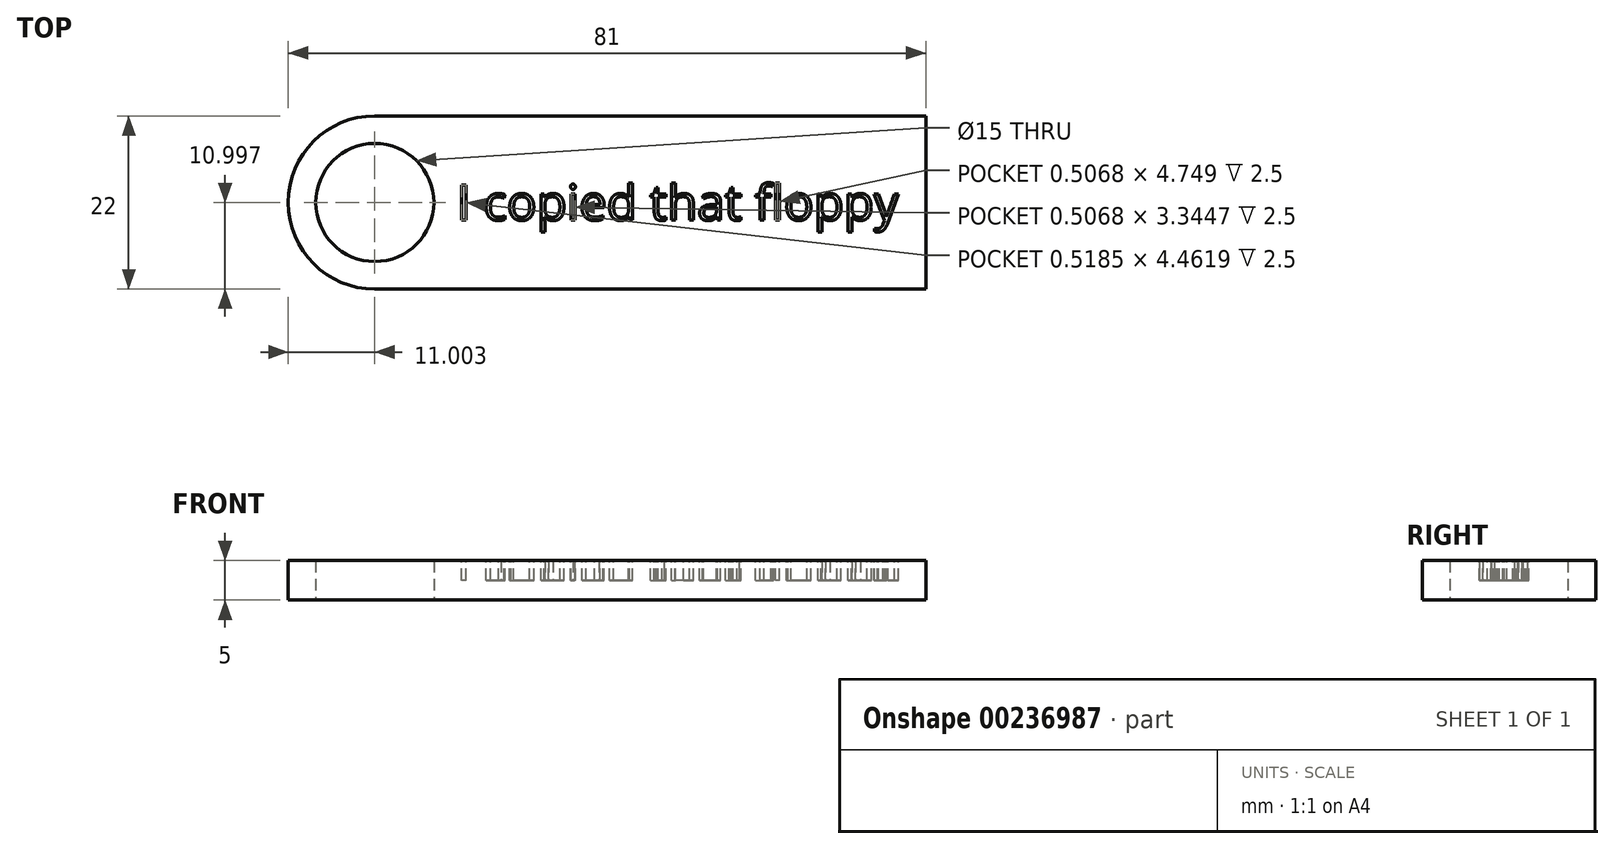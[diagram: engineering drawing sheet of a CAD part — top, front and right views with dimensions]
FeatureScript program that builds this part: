
annotation { "Feature Type Name" : "Feature", "Feature Type Description" : "" }
export const myFeature = defineFeature(function(context is Context, id is Id, definition is map)
    precondition{}
    {
        {
            var Q0;
            Q0=qCreatedBy(makeId("Top.planeOp"),FACE);
            var sketch = newSketch(context, id + "F0", { "sketchPlane" : qUnion([Q0])});
            skLineSegment(sketch, "E0", {"start": v(39.9, 37.37) * mm, "end": v(-30.1, 37.37) * mm});
            skLineSegment(sketch, "E1", {"start": v(39.9, 37.37) * mm, "end": v(39.9, 15.37) * mm});
            skLineSegment(sketch, "E2", {"start": v(39.9, 15.37) * mm, "end": v(-30.1, 15.37) * mm});
            skArc(sketch, "E3", {"start": v(-30.1, 37.37) * mm, "mid": v(-41.1, 26.37) * mm, "end": v(-30.1, 15.37) * mm});
            skCircle(sketch, "E4", {"center": v(-30.1, 26.37) * mm, "radius": 7.5 * mm});
            skSolve(sketch);
        }
        {
            var Q0;
            Q0=makeQuery(id+"F0.imprint","IMPRINT",FACE,{"disambiguationData":[TD([[makeQuery(id+"F0.imprint","IMPRINT",EDGE,{"derivedFrom":sQuery(id+"F0.wireOp",EDGE,"E0")}),1.0]])]});
            extrude(context, id + "F1", {"entities" : qUnion([Q0]), "depth" : 5 * mm});
        }
        {
            var Q0;
            Q0=makeQuery(id+"F1.opExtrude","CAP_FACE",FACE,{"disambiguationData":[OSD([sQuery(id+"F0.wireOp",EDGE,"E0"),sQuery(id+"F0.wireOp",EDGE,"E1"),sQuery(id+"F0.wireOp",EDGE,"E2"),sQuery(id+"F0.wireOp",EDGE,"E3"),sQuery(id+"F0.wireOp",EDGE,"E4")])],"isStart":false});
            var sketch = newSketch(context, id + "F2", { "sketchPlane" : qUnion([Q0])});
            skText(sketch, "E5", { "text": "I copied that floppy", "fontName": "OpenSans-Regular.ttf"});
            const initialGuessF2  = {"E5": [-0.01966, 0.02412, 1, 0, 0.0045]};
            skSetInitialGuess(sketch, initialGuessF2);
            skSolve(sketch);
        }
        {
            var Q0;
            Q0 = qSketchRegion(id + "F2", true);
            extrude(context, id + "F3", {"entities" : qUnion([Q0]), "operationType" : NewBodyOperationType.REMOVE, "oppositeDirection" : true, "depth" : 2.5 * mm});
        }
    });
